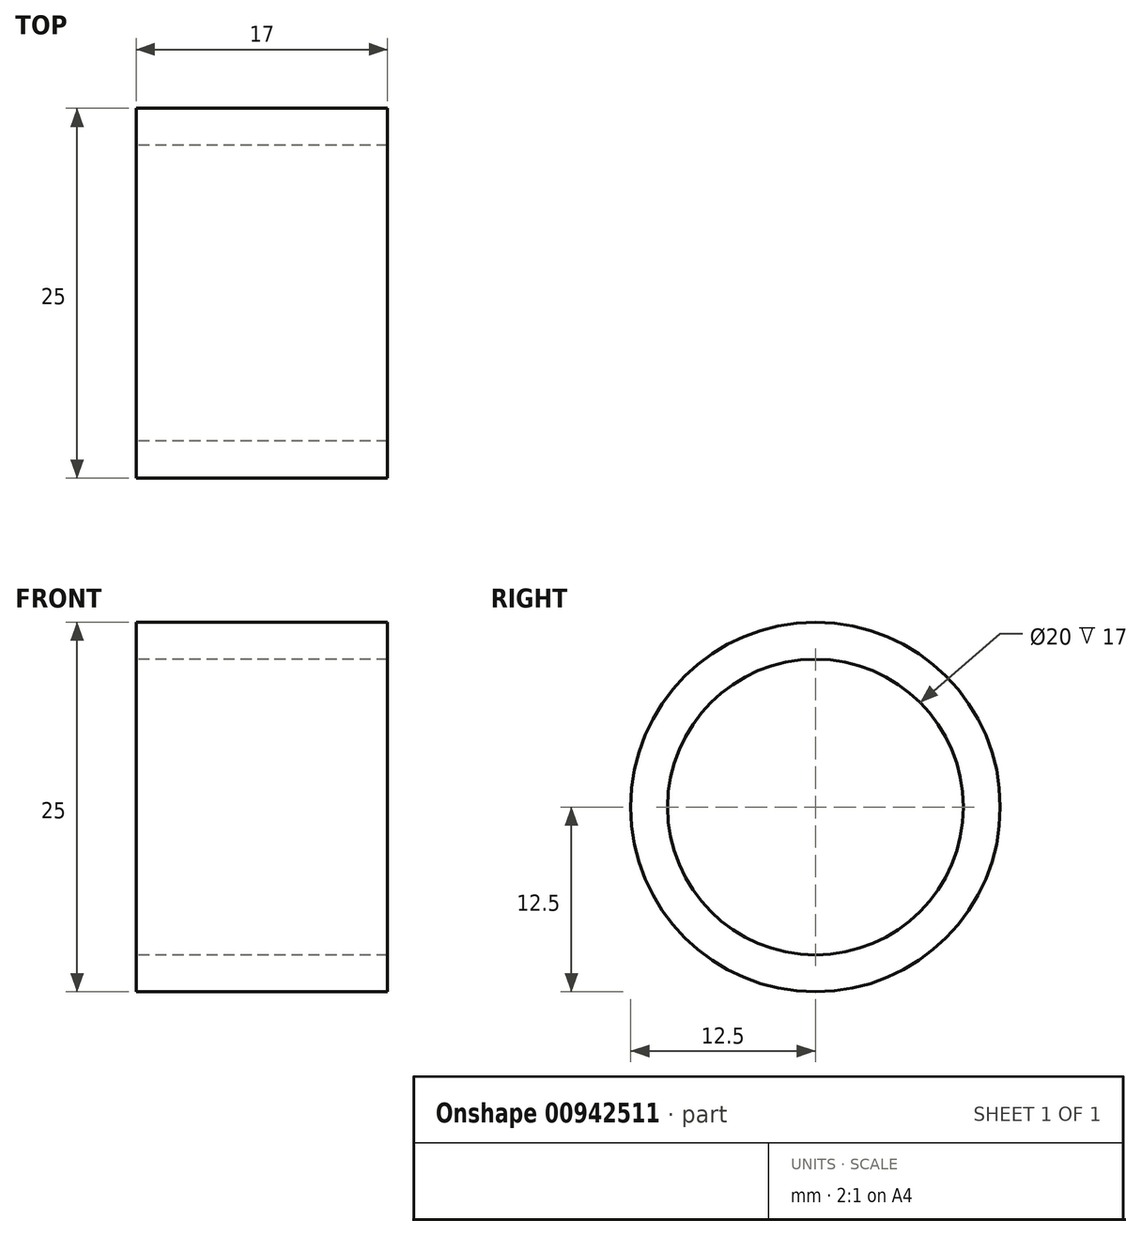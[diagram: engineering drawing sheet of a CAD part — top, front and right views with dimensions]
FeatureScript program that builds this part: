
annotation { "Feature Type Name" : "Feature", "Feature Type Description" : "" }
export const myFeature = defineFeature(function(context is Context, id is Id, definition is map)
    precondition{}
    {
        {
            var Q0;
            Q0=qCreatedBy(makeId("Right.planeOp"),FACE);
            var sketch = newSketch(context, id + "F0", { "sketchPlane" : qUnion([Q0])});
            skCircle(sketch, "E0", {"center": v(0, 0) * mm, "radius": 12.5 * mm});
            skCircle(sketch, "E1", {"center": v(0, 0) * mm, "radius": 10 * mm});
            skSolve(sketch);
        }
        {
            var Q0;
            Q0=makeQuery(id+"F0.imprint","IMPRINT",FACE,{"disambiguationData":[TD([[makeQuery(id+"F0.imprint","IMPRINT",EDGE,{"derivedFrom":sQuery(id+"F0.wireOp",EDGE,"E0")}),1.0]])]});
            extrude(context, id + "F1", {"entities" : qUnion([Q0]), "depth" : 17 * mm, "offsetDistance" : 25.4 * mm});
        }
    });
